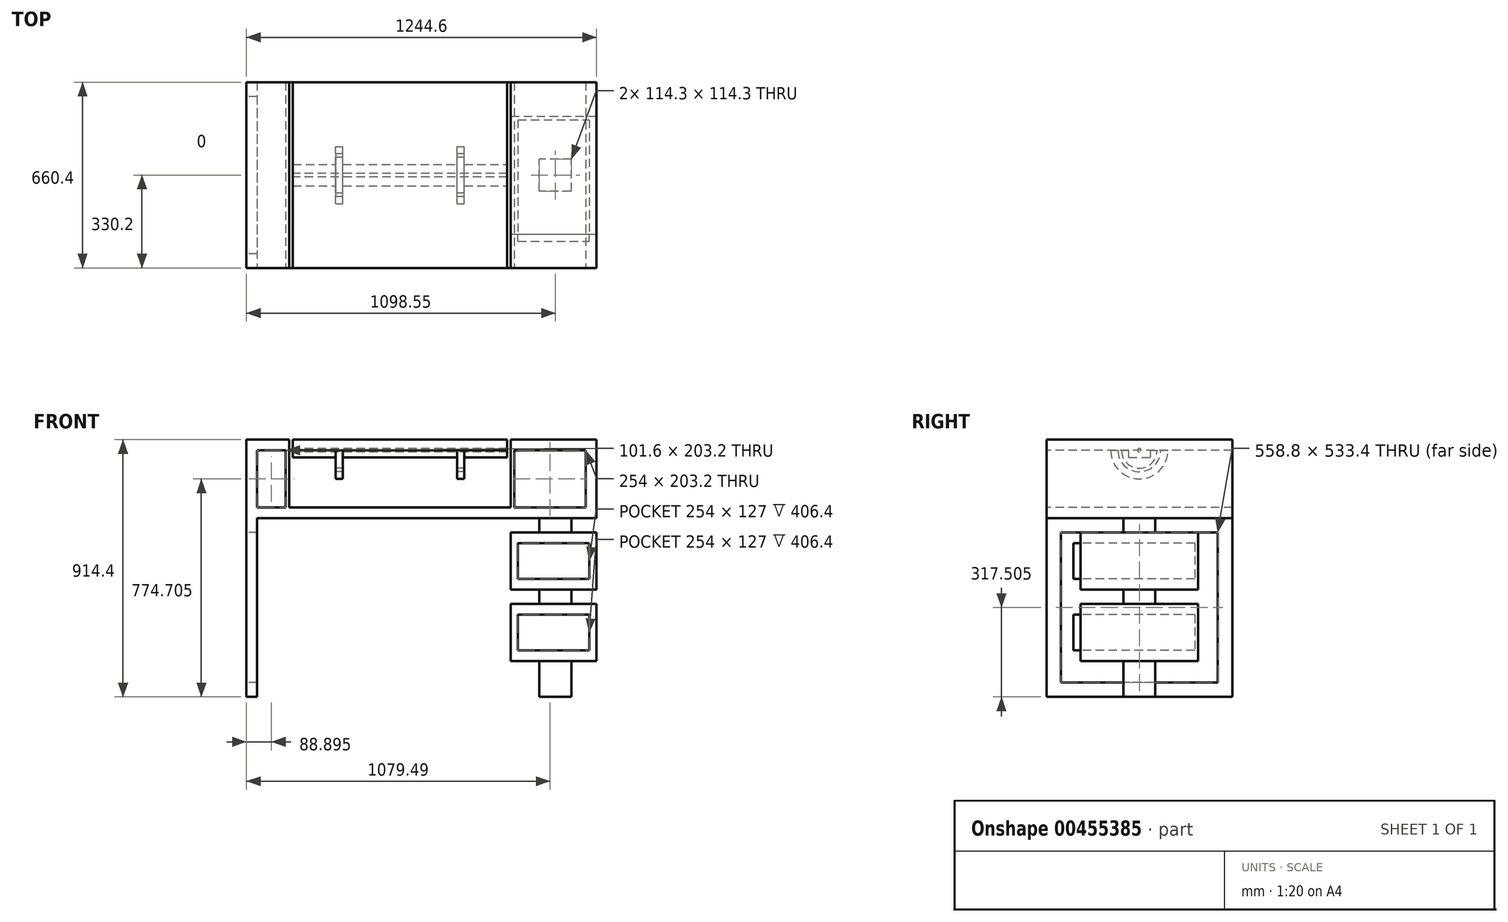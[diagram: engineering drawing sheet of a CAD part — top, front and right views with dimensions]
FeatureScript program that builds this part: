
annotation { "Feature Type Name" : "Feature", "Feature Type Description" : "" }
export const myFeature = defineFeature(function(context is Context, id is Id, definition is map)
    precondition{}
    {
        {
            var Q0;
            Q0=qCreatedBy(makeId("Front.planeOp"),FACE);
            var sketch = newSketch(context, id + "F0", { "sketchPlane" : qUnion([Q0])});
            skLineSegment(sketch, "E0.bottom", {"start": v(-63.62, 424.58) * mm, "end": v(-216.02, 424.58) * mm});
            skLineSegment(sketch, "E0.top", {"start": v(-63.62, 386.48) * mm, "end": v(-177.92, 386.48) * mm});
            skLineSegment(sketch, "E0.left", {"start": v(-63.62, 424.58) * mm, "end": v(-63.62, 386.48) * mm});
            skLineSegment(sketch, "E1", {"start": v(-177.92, 386.48) * mm, "end": v(-177.92, 399.18) * mm});
            skLineSegment(sketch, "E2", {"start": v(-177.92, 399.18) * mm, "end": v(-190.62, 399.18) * mm});
            skLineSegment(sketch, "E3", {"start": v(-190.62, 399.18) * mm, "end": v(-190.62, 386.48) * mm});
            skLineSegment(sketch, "E4", {"start": v(-190.62, 386.48) * mm, "end": v(-196.97, 386.48) * mm});
            skLineSegment(sketch, "E5", {"start": v(-196.97, 386.48) * mm, "end": v(-196.97, 399.18) * mm});
            skLineSegment(sketch, "E6", {"start": v(-196.97, 399.18) * mm, "end": v(-209.67, 399.18) * mm});
            skLineSegment(sketch, "E7", {"start": v(-209.67, 386.48) * mm, "end": v(-216.02, 386.48) * mm});
            skLineSegment(sketch, "E8", {"start": v(-216.02, 386.48) * mm, "end": v(-216.02, 424.58) * mm});
            skLineSegment(sketch, "E9", {"start": v(-209.67, 399.18) * mm, "end": v(-196.97, 399.18) * mm});
            skLineSegment(sketch, "E10", {"start": v(-216.02, 386.48) * mm, "end": v(-209.67, 386.48) * mm});
            skLineSegment(sketch, "E11", {"start": v(-209.67, 386.48) * mm, "end": v(-209.67, 399.18) * mm});
            skLineSegment(sketch, "E12", {"start": v(-196.97, 399.18) * mm, "end": v(-196.97, 386.48) * mm});
            skLineSegment(sketch, "E13", {"start": v(-196.97, 386.48) * mm, "end": v(-190.62, 386.48) * mm});
            skLineSegment(sketch, "E14", {"start": v(-190.62, 386.48) * mm, "end": v(-190.62, 399.18) * mm});
            skLineSegment(sketch, "E15", {"start": v(-190.62, 399.18) * mm, "end": v(-177.92, 399.18) * mm});
            skLineSegment(sketch, "E16", {"start": v(-177.92, 399.18) * mm, "end": v(-177.92, 386.48) * mm});
            skLineSegment(sketch, "E17", {"start": v(-209.67, 399.18) * mm, "end": v(-209.67, 386.48) * mm});
            skLineSegment(sketch, "E18", {"start": v(-177.92, 386.48) * mm, "end": v(-177.92, -489.82) * mm});
            skLineSegment(sketch, "E19", {"start": v(-177.92, -489.82) * mm, "end": v(-216.02, -489.82) * mm});
            skLineSegment(sketch, "E20", {"start": v(-216.02, -489.82) * mm, "end": v(-216.02, 386.48) * mm});
            skLineSegment(sketch, "E21.bottom", {"start": v(-50.92, 424.58) * mm, "end": v(711.08, 424.58) * mm});
            skLineSegment(sketch, "E21.top", {"start": v(-50.92, 386.48) * mm, "end": v(711.08, 386.48) * mm});
            skLineSegment(sketch, "E21.left", {"start": v(-50.92, 424.58) * mm, "end": v(-50.92, 386.48) * mm});
            skLineSegment(sketch, "E21.right", {"start": v(711.08, 424.58) * mm, "end": v(711.08, 386.48) * mm});
            skLineSegment(sketch, "E22.left", {"start": v(-63.62, 386.48) * mm, "end": v(-63.62, 183.28) * mm});
            skLineSegment(sketch, "E23.bottom", {"start": v(-177.92, 386.48) * mm, "end": v(-76.32, 386.48) * mm});
            skLineSegment(sketch, "E23.left", {"start": v(-177.92, 386.48) * mm, "end": v(-177.92, 221.38) * mm});
            skLineSegment(sketch, "E23.right", {"start": v(-76.32, 386.48) * mm, "end": v(-76.32, 183.28) * mm});
            skLineSegment(sketch, "E24.bottom", {"start": v(723.78, 424.58) * mm, "end": v(1028.58, 424.58) * mm});
            skLineSegment(sketch, "E24.left", {"start": v(723.78, 424.58) * mm, "end": v(723.78, 386.48) * mm});
            skLineSegment(sketch, "E25", {"start": v(-63.62, 183.28) * mm, "end": v(-76.32, 183.28) * mm});
            skLineSegment(sketch, "E26.bottom", {"start": v(723.78, 386.48) * mm, "end": v(736.48, 386.48) * mm});
            skLineSegment(sketch, "E26.top", {"start": v(723.78, 183.28) * mm, "end": v(736.48, 183.28) * mm});
            skLineSegment(sketch, "E26.left", {"start": v(723.78, 386.48) * mm, "end": v(723.78, 183.28) * mm});
            skLineSegment(sketch, "E26.right", {"start": v(736.48, 386.48) * mm, "end": v(736.48, 183.28) * mm});
            skLineSegment(sketch, "E27.bottom", {"start": v(-177.92, 183.28) * mm, "end": v(990.48, 183.28) * mm});
            skLineSegment(sketch, "E27.top", {"start": v(-177.92, 145.18) * mm, "end": v(990.48, 145.18) * mm});
            skLineSegment(sketch, "E27.left", {"start": v(-177.92, 183.28) * mm, "end": v(-177.92, 145.18) * mm});
            skLineSegment(sketch, "E27.right", {"start": v(990.48, 183.28) * mm, "end": v(990.48, 145.18) * mm});
            skLineSegment(sketch, "E28", {"start": v(1009.53, 386.48) * mm, "end": v(1009.53, 399.18) * mm});
            skLineSegment(sketch, "E29", {"start": v(1009.53, 386.48) * mm, "end": v(1003.18, 386.48) * mm});
            skLineSegment(sketch, "E30", {"start": v(1003.18, 386.48) * mm, "end": v(1003.18, 399.18) * mm});
            skLineSegment(sketch, "E31", {"start": v(1003.18, 399.18) * mm, "end": v(990.48, 399.18) * mm});
            skLineSegment(sketch, "E32", {"start": v(990.48, 399.18) * mm, "end": v(990.48, 386.48) * mm});
            skLineSegment(sketch, "E33", {"start": v(990.48, 386.48) * mm, "end": v(723.78, 386.48) * mm});
            skLineSegment(sketch, "E34", {"start": v(1009.53, 399.18) * mm, "end": v(1022.23, 399.18) * mm});
            skLineSegment(sketch, "E35", {"start": v(1022.23, 399.18) * mm, "end": v(1022.23, 386.48) * mm});
            skLineSegment(sketch, "E36", {"start": v(1028.58, 424.58) * mm, "end": v(1028.58, 386.48) * mm});
            skLineSegment(sketch, "E37", {"start": v(1028.58, 386.48) * mm, "end": v(1022.23, 386.48) * mm});
            skLineSegment(sketch, "E38", {"start": v(1022.23, 386.48) * mm, "end": v(1022.23, 399.18) * mm});
            skLineSegment(sketch, "E39", {"start": v(1022.23, 399.18) * mm, "end": v(1009.53, 399.18) * mm});
            skLineSegment(sketch, "E40", {"start": v(1009.53, 399.18) * mm, "end": v(1009.53, 386.48) * mm});
            skLineSegment(sketch, "E41", {"start": v(990.48, 399.18) * mm, "end": v(990.48, 145.18) * mm});
            skPoint(sketch, "E41.endSnap0", {"position": v(990.48, 392.83) * mm});
            skLineSegment(sketch, "E42", {"start": v(990.48, 145.18) * mm, "end": v(1028.58, 145.18) * mm});
            skLineSegment(sketch, "E43", {"start": v(1028.58, 145.18) * mm, "end": v(1028.58, 386.48) * mm});
            skSolve(sketch);
        }
        {
            var Q0;
            Q0 = qSketchRegion(id + "F0", true);
            extrude(context, id + "F1", {"entities" : qUnion([Q0]), "oppositeDirection" : true, "depth" : 660.4 * mm});
        }
        {
            var Q0;
            Q0=makeQuery(id+"F1.opExtrude","SWEPT_FACE",FACE,{"disambiguationData":[OSD([sQuery(id+"F0.wireOp",EDGE,"E36"),sQuery(id+"F0.wireOp",EDGE,"E43")])]});
            var sketch = newSketch(context, id + "F2", { "sketchPlane" : qUnion([Q0])});
            skSolve(sketch);
        }
        {
            var Q0;
            Q0=makeQuery(id+"F1.opExtrude","SWEPT_FACE",FACE,{"disambiguationData":[OSD([sQuery(id+"F0.wireOp",EDGE,"E8"),sQuery(id+"F0.wireOp",EDGE,"E20")])]});
            var sketch = newSketch(context, id + "F3", { "sketchPlane" : qUnion([Q0])});
            skLineSegment(sketch, "E44.bottom", {"start": v(-609.6, -439.02) * mm, "end": v(-50.8, -439.02) * mm});
            skLineSegment(sketch, "E44.top", {"start": v(-609.6, 94.38) * mm, "end": v(-50.8, 94.38) * mm});
            skLineSegment(sketch, "E44.left", {"start": v(-609.6, -439.02) * mm, "end": v(-609.6, 94.38) * mm});
            skLineSegment(sketch, "E44.right", {"start": v(-50.8, -439.02) * mm, "end": v(-50.8, 94.38) * mm});
            skSolve(sketch);
        }
        {
            var Q0;
            Q0=makeQuery(id+"F3.imprint","IMPRINT",FACE,{"disambiguationData":[TD([[makeQuery(id+"F3.imprint","IMPRINT",EDGE,{"derivedFrom":sQuery(id+"F3.wireOp",EDGE,"E44.bottom")}),1.0]])]});
            extrude(context, id + "F4", {"entities" : qUnion([Q0]), "operationType" : NewBodyOperationType.REMOVE, "oppositeDirection" : true, "depth" : 38.1 * mm});
        }
        {
            var Q0;
            Q0=makeQuery(id+"F1.opExtrude","SWEPT_FACE",FACE,{"disambiguationData":[OSD([sQuery(id+"F0.wireOp",EDGE,"E27.top"),sQuery(id+"F0.wireOp",EDGE,"E42")])]});
            var sketch = newSketch(context, id + "F5", { "sketchPlane" : qUnion([Q0])});
            skSolve(sketch);
        }
        {
            var Q0;
            {var subQ1=sQuery(id+"F0.wireOp",EDGE,"E42");Q0=makeQuery(id+"F5.imprint","IMPRINT",FACE,{"disambiguationData":[TD([[makeQuery(id+"F5.imprint","IMPRINT",EDGE,{"derivedFrom":makeQuery(id+"F1.opExtrude","SWEPT_EDGE",EDGE,{"disambiguationData":[OSD([subQ1,sQuery(id+"F0.wireOp",EDGE,"E43")])]})}),1.0]])]});}
            var sketch = newSketch(context, id + "F6", { "sketchPlane" : qUnion([Q0])});
            skLineSegment(sketch, "E45.bottom", {"start": v(939.68, -273.05) * mm, "end": v(825.38, -273.05) * mm});
            skLineSegment(sketch, "E45.top", {"start": v(939.68, -387.35) * mm, "end": v(825.38, -387.35) * mm});
            skLineSegment(sketch, "E45.left", {"start": v(939.68, -273.05) * mm, "end": v(939.68, -387.35) * mm});
            skLineSegment(sketch, "E45.right", {"start": v(825.38, -273.05) * mm, "end": v(825.38, -387.35) * mm});
            skSolve(sketch);
        }
        {
            var Q0;
            Q0 = qSketchRegion(id + "F6", true);
            extrude(context, id + "F7", {"entities" : qUnion([Q0]), "operationType" : NewBodyOperationType.ADD, "depth" : 635 * mm});
        }
        {
            var Q0;
            {var subQ0=sQuery(id+"F0.wireOp",EDGE,"E36");Q0=makeQuery(id+"F2.imprint","IMPRINT",FACE,{"disambiguationData":[TD([[makeQuery(id+"F2.imprint","IMPRINT",EDGE,{"derivedFrom":makeQuery(id+"F1.opExtrude","SWEPT_EDGE",EDGE,{"disambiguationData":[OSD([sQuery(id+"F0.wireOp",EDGE,"E24.bottom"),subQ0])]})}),1.0]])]});}
            var sketch = newSketch(context, id + "F8", { "sketchPlane" : qUnion([Q0])});
            skLineSegment(sketch, "E46.bottom", {"start": v(120.65, 94.38) * mm, "end": v(539.75, 94.38) * mm});
            skLineSegment(sketch, "E46.top", {"start": v(120.65, -108.82) * mm, "end": v(539.75, -108.82) * mm});
            skLineSegment(sketch, "E46.left", {"start": v(120.65, 94.38) * mm, "end": v(120.65, -108.82) * mm});
            skLineSegment(sketch, "E46.right", {"start": v(539.75, 94.38) * mm, "end": v(539.75, -108.82) * mm});
            skLineSegment(sketch, "E47.bottom", {"start": v(120.65, -159.62) * mm, "end": v(539.75, -159.62) * mm});
            skLineSegment(sketch, "E47.top", {"start": v(120.65, -362.82) * mm, "end": v(539.75, -362.82) * mm});
            skLineSegment(sketch, "E47.left", {"start": v(120.65, -159.62) * mm, "end": v(120.65, -362.82) * mm});
            skLineSegment(sketch, "E47.right", {"start": v(539.75, -159.62) * mm, "end": v(539.75, -362.82) * mm});
            skSolve(sketch);
        }
        {
            var Q0;
            Q0 = qSketchRegion(id + "F8", true);
            extrude(context, id + "F9", {"entities" : qUnion([Q0]), "operationType" : NewBodyOperationType.ADD, "oppositeDirection" : true, "depth" : 304.8 * mm});
        }
        {
            var Q0;
            Q0=makeQuery(id+"F9.opExtrude","SWEPT_FACE",FACE,{"disambiguationData":[OSD([sQuery(id+"F8.wireOp",EDGE,"E46.left")])]});
            var sketch = newSketch(context, id + "F10", { "sketchPlane" : qUnion([Q0])});
            skLineSegment(sketch, "E48.bottom", {"start": v(749.18, 56.28) * mm, "end": v(1003.18, 56.28) * mm});
            skLineSegment(sketch, "E48.top", {"start": v(749.18, -70.72) * mm, "end": v(1003.18, -70.72) * mm});
            skLineSegment(sketch, "E48.left", {"start": v(749.18, 56.28) * mm, "end": v(749.18, -70.72) * mm});
            skLineSegment(sketch, "E48.right", {"start": v(1003.18, 56.28) * mm, "end": v(1003.18, -70.72) * mm});
            skLineSegment(sketch, "E49.bottom", {"start": v(749.18, -197.72) * mm, "end": v(1003.18, -197.72) * mm});
            skLineSegment(sketch, "E49.top", {"start": v(749.18, -324.72) * mm, "end": v(1003.18, -324.72) * mm});
            skLineSegment(sketch, "E49.left", {"start": v(749.18, -197.72) * mm, "end": v(749.18, -324.72) * mm});
            skLineSegment(sketch, "E49.right", {"start": v(1003.18, -197.72) * mm, "end": v(1003.18, -324.72) * mm});
            skSolve(sketch);
        }
        {
            var Q0;
            Q0 = qSketchRegion(id + "F10", true);
            extrude(context, id + "F11", {"entities" : qUnion([Q0]), "operationType" : NewBodyOperationType.ADD, "depth" : 25.4 * mm});
        }
        {
            var Q0;
            Q0 = qSketchRegion(id + "F10", true);
            extrude(context, id + "F12", {"entities" : qUnion([Q0]), "operationType" : NewBodyOperationType.REMOVE, "oppositeDirection" : true, "depth" : 406.4 * mm});
        }
        {
            var Q0;
            Q0=makeQuery(id+"F1.opExtrude","SWEPT_FACE",FACE,{"disambiguationData":[OSD([sQuery(id+"F0.wireOp",EDGE,"E21.top")])]});
            var sketch = newSketch(context, id + "F13", { "sketchPlane" : qUnion([Q0])});
            skLineSegment(sketch, "E50.bottom", {"start": v(101.48, -228.6) * mm, "end": v(126.88, -228.6) * mm});
            skLineSegment(sketch, "E50.top", {"start": v(101.48, -431.8) * mm, "end": v(126.88, -431.8) * mm});
            skLineSegment(sketch, "E50.left", {"start": v(101.48, -228.6) * mm, "end": v(101.48, -431.8) * mm});
            skLineSegment(sketch, "E50.right", {"start": v(126.88, -228.6) * mm, "end": v(126.88, -431.8) * mm});
            skLineSegment(sketch, "E51.bottom", {"start": v(533.28, -228.6) * mm, "end": v(558.68, -228.6) * mm});
            skLineSegment(sketch, "E51.top", {"start": v(533.28, -431.8) * mm, "end": v(558.68, -431.8) * mm});
            skLineSegment(sketch, "E51.left", {"start": v(533.28, -228.6) * mm, "end": v(533.28, -431.8) * mm});
            skLineSegment(sketch, "E51.right", {"start": v(558.68, -228.6) * mm, "end": v(558.68, -431.8) * mm});
            skSolve(sketch);
        }
        {
            var Q0;
            Q0 = qSketchRegion(id + "F13", true);
            extrude(context, id + "F14", {"entities" : qUnion([Q0]), "operationType" : NewBodyOperationType.ADD, "depth" : 101.6 * mm});
        }
        {
            var Q0;
            Q0=makeQuery(id+"F14.opExtrude","CAP_EDGE",EDGE,{"disambiguationData":[OSD([sQuery(id+"F13.wireOp",EDGE,"E51.bottom")])],"isStart":false});
            var Q1;
            Q1=makeQuery(id+"F14.opExtrude","CAP_EDGE",EDGE,{"disambiguationData":[OSD([sQuery(id+"F13.wireOp",EDGE,"E51.top")])],"isStart":false});
            var Q2;
            Q2=makeQuery(id+"F14.opExtrude","CAP_EDGE",EDGE,{"disambiguationData":[OSD([sQuery(id+"F13.wireOp",EDGE,"E50.bottom")])],"isStart":false});
            var Q3;
            Q3=makeQuery(id+"F14.opExtrude","CAP_EDGE",EDGE,{"disambiguationData":[OSD([sQuery(id+"F13.wireOp",EDGE,"E50.top")])],"isStart":false});
            fillet(context, id + "F15", {"entities" : qUnion([Q0, Q1, Q2, Q3]), "radius" : 101.6 * mm, "tangentPropagation" : true, "allowEdgeOverflow" : false});
        }
        {
            var Q0;
            Q0=makeQuery(id+"F14.opExtrude","SWEPT_FACE",FACE,{"disambiguationData":[OSD([sQuery(id+"F13.wireOp",EDGE,"E50.left")])]});
            var sketch = newSketch(context, id + "F16", { "sketchPlane" : qUnion([Q0])});
            skArc(sketch, "E52", {"start": v(-406.4, 386.48) * mm, "mid": v(-330.2, 310.28) * mm, "end": v(-254, 386.48) * mm});
            skArc(sketch, "E53", {"start": v(-393.7, 386.48) * mm, "mid": v(-330.2, 322.98) * mm, "end": v(-266.7, 386.48) * mm});
            skLineSegment(sketch, "E54", {"start": v(-393.7, 386.48) * mm, "end": v(-406.4, 386.48) * mm});
            skLineSegment(sketch, "E55", {"start": v(-266.7, 386.48) * mm, "end": v(-254, 386.48) * mm});
            skCircle(sketch, "E56", {"center": v(-330.2, 386.48) * mm, "radius": 6.35 * mm});
            skSolve(sketch);
        }
        {
            var Q0;
            {var subQ2=sQuery(id+"F0.wireOp",EDGE,"E21.right");var subQ3=sQuery(id+"F0.wireOp",EDGE,"E21.left");var subQ4=sQuery(id+"F0.wireOp",EDGE,"E21.top");var subQ8=makeQuery(id+"FdWVpAXv5SxHgQB_2.opExtrude","SWEPT_FACE",FACE,{"disambiguationData":[OSD([sQuery(id+"F16.wireOp",EDGE,"E54")])]});var subQ9=makeQuery(id+"F1.opExtrude","SWEPT_FACE",FACE,{"disambiguationData":[OSD([subQ4])]});var subQ10=makeQuery(id+"FdWVpAXv5SxHgQB_2.opExtrude","SWEPT_FACE",FACE,{"disambiguationData":[OSD([sQuery(id+"F16.wireOp",EDGE,"E55")])]});Q0=makeQuery(id+"FbDQFoXMD2D6nUd_2.boolean.opBoolean","SPLIT",FACE,{"disambiguationData":[TD([makeQuery(id+"F1.opExtrude","CAP_FACE",FACE,{"disambiguationData":[OSD([sQuery(id+"F0.wireOp",EDGE,"E21.bottom"),subQ4,subQ3,subQ2])],"isStart":true})])],"derivedFrom":makeQuery(id+"FdWVpAXv5SxHgQB_2.boolean.opBoolean","MERGE",FACE,{"derivedFrom":[subQ9,subQ8,subQ10]})});}
            var sketch = newSketch(context, id + "F17", { "sketchPlane" : qUnion([Q0])});
            skLineSegment(sketch, "E57.bottom", {"start": v(-50.92, -292.1) * mm, "end": v(711.08, -292.1) * mm});
            skLineSegment(sketch, "E57.top", {"start": v(-50.92, -368.3) * mm, "end": v(711.08, -368.3) * mm});
            skLineSegment(sketch, "E57.left", {"start": v(-50.92, -292.1) * mm, "end": v(-50.92, -368.3) * mm});
            skLineSegment(sketch, "E57.right", {"start": v(711.08, -292.1) * mm, "end": v(711.08, -368.3) * mm});
            skSolve(sketch);
        }
        {
            var Q0;
            Q0 = qSketchRegion(id + "F17", true);
            extrude(context, id + "F18", {"entities" : qUnion([Q0]), "operationType" : NewBodyOperationType.ADD, "depth" : 25.4 * mm});
        }
        {
            var Q0;
            Q0 = qSketchRegion(id + "F16", true);
            extrude(context, id + "F19", {"entities" : qUnion([Q0]), "operationType" : NewBodyOperationType.REMOVE, "oppositeDirection" : true, "depth" : 609.6 * mm});
        }
        {
            var Q0;
            Q0 = qSketchRegion(id + "F16", true);
            extrude(context, id + "F20", {"entities" : qUnion([Q0]), "operationType" : NewBodyOperationType.REMOVE, "depth" : 152.4 * mm});
        }
        {
            var Q0;
            Q0=makeQuery(id+"F1.opExtrude","SWEPT_BODY",BODY,{"disambiguationData":[OSD([sQuery(id+"F0.wireOp",EDGE,"E21.bottom"),sQuery(id+"F0.wireOp",EDGE,"E21.top"),sQuery(id+"F0.wireOp",EDGE,"E21.left"),sQuery(id+"F0.wireOp",EDGE,"E21.right")])]});
            transform(context, id + "F21", {"entities" : qUnion([Q0]), "transformType" : TransformType.TRANSLATION_3D, "dx" : 0 * mm, "dy" : 0 * mm, "dz" : 0 * mm, "makeCopy" : true});
        }
    });
